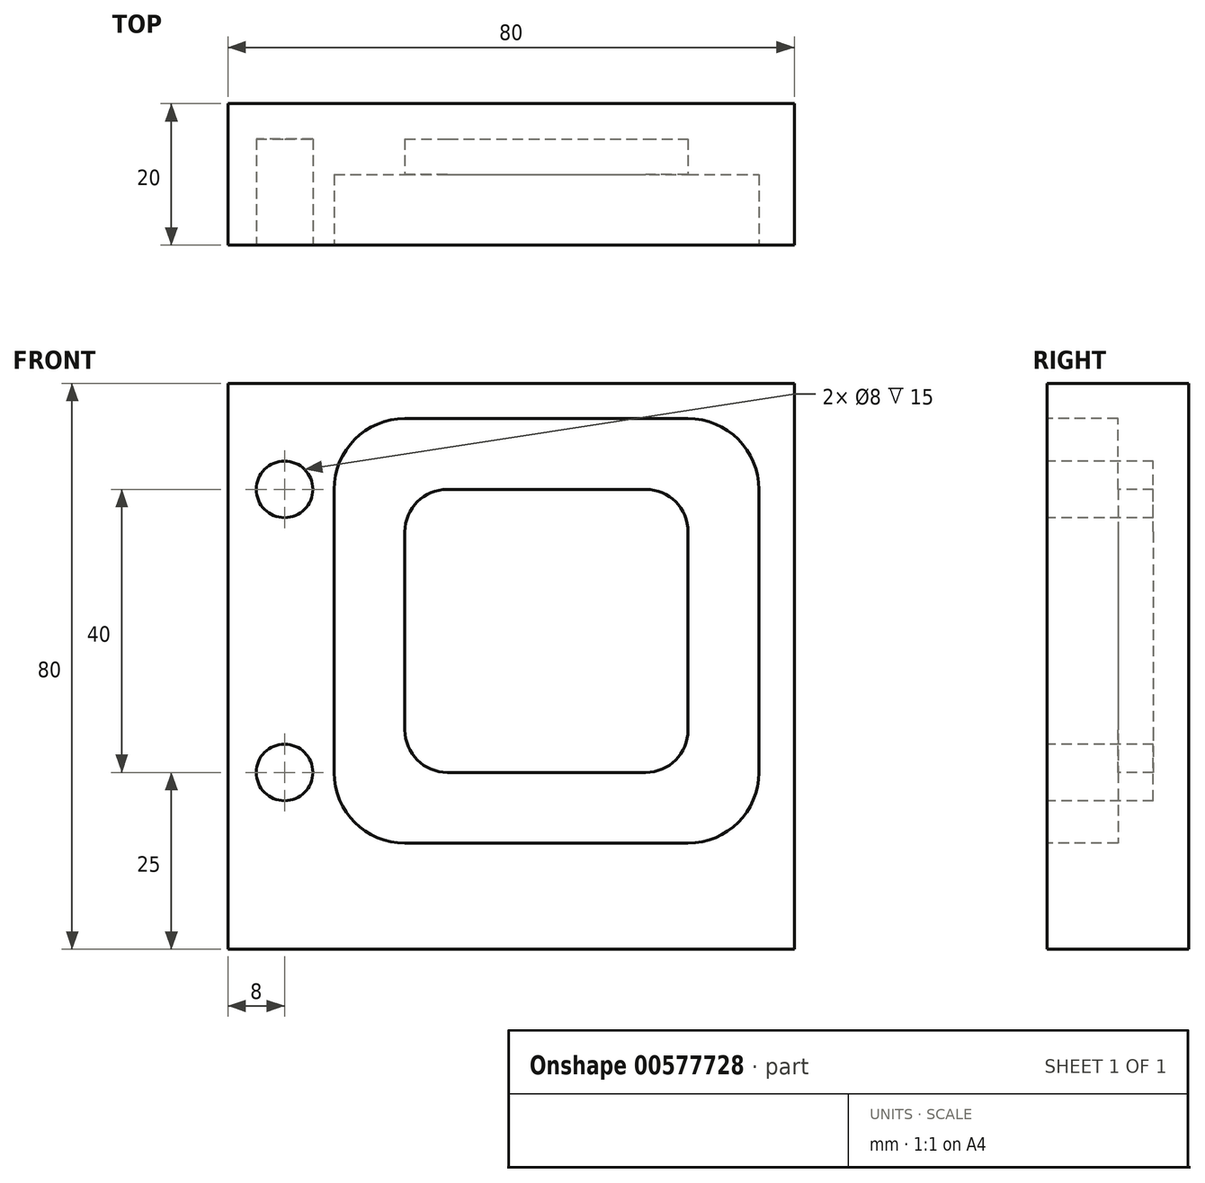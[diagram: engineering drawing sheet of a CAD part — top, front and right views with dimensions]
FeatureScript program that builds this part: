
annotation { "Feature Type Name" : "Feature", "Feature Type Description" : "" }
export const myFeature = defineFeature(function(context is Context, id is Id, definition is map)
    precondition{}
    {
        {
            var Q0;
            Q0=qCreatedBy(makeId("Front.planeOp"),FACE);
            var sketch = newSketch(context, id + "F0", { "sketchPlane" : qUnion([Q0])});
            skLineSegment(sketch, "E0.bottom", {"start": v(0, 0) * mm, "end": v(-80, 0) * mm});
            skLineSegment(sketch, "E0.top", {"start": v(0, 80) * mm, "end": v(-80, 80) * mm});
            skLineSegment(sketch, "E0.left", {"start": v(0, 0) * mm, "end": v(0, 80) * mm});
            skLineSegment(sketch, "E0.right", {"start": v(-80, 0) * mm, "end": v(-80, 80) * mm});
            skSolve(sketch);
        }
        {
            var Q0;
            Q0=makeQuery(id+"F0.imprint","IMPRINT",FACE,{"disambiguationData":[TD([[makeQuery(id+"F0.imprint","IMPRINT",EDGE,{"derivedFrom":sQuery(id+"F0.wireOp",EDGE,"E0.bottom")}),-1.0]])]});
            extrude(context, id + "F1", {"entities" : qUnion([Q0]), "depth" : 20 * mm, "offsetDistance" : 25 * mm});
        }
        {
            var Q0;
            Q0=makeQuery(id+"F1.opExtrude","CAP_FACE",FACE,{"disambiguationData":[OSD([sQuery(id+"F0.wireOp",EDGE,"E0.bottom"),sQuery(id+"F0.wireOp",EDGE,"E0.top"),sQuery(id+"F0.wireOp",EDGE,"E0.left"),sQuery(id+"F0.wireOp",EDGE,"E0.right")])],"isStart":false});
            var sketch = newSketch(context, id + "F2", { "sketchPlane" : qUnion([Q0])});
            skLineSegment(sketch, "E1", {"start": v(-55, 75) * mm, "end": v(-15, 75) * mm});
            skLineSegment(sketch, "E2", {"start": v(-65, 65) * mm, "end": v(-65, 25) * mm});
            skLineSegment(sketch, "E3", {"start": v(-55, 15) * mm, "end": v(-15, 15) * mm});
            skLineSegment(sketch, "E4", {"start": v(-5, 65) * mm, "end": v(-5, 25) * mm});
            skArc(sketch, "E5", {"start": v(-55, 75) * mm, "mid": v(-62.07, 72.07) * mm, "end": v(-65, 65) * mm});
            skArc(sketch, "E6", {"start": v(-65, 25) * mm, "mid": v(-62.07, 17.93) * mm, "end": v(-55, 15) * mm});
            skArc(sketch, "E7", {"start": v(-15, 15) * mm, "mid": v(-7.93, 17.93) * mm, "end": v(-5, 25) * mm});
            skArc(sketch, "E8", {"start": v(-5, 65) * mm, "mid": v(-7.93, 72.07) * mm, "end": v(-15, 75) * mm});
            skSolve(sketch);
        }
        {
            var Q0;
            Q0=makeQuery(id+"F2.imprint","IMPRINT",FACE,{"disambiguationData":[TD([[makeQuery(id+"F2.imprint","IMPRINT",EDGE,{"derivedFrom":sQuery(id+"F2.wireOp",EDGE,"E1")}),-1.0]])]});
            extrude(context, id + "F3", {"entities" : qUnion([Q0]), "operationType" : NewBodyOperationType.REMOVE, "oppositeDirection" : true, "depth" : 10 * mm, "offsetDistance" : 25 * mm});
        }
        {
            var Q0;
            Q0=makeQuery(id+"F3.boolean.opBoolean","COPY",FACE,{"derivedFrom":makeQuery(id+"F3.opExtrude","CAP_FACE",FACE,{"disambiguationData":[OSD([sQuery(id+"F2.wireOp",EDGE,"E1"),sQuery(id+"F2.wireOp",EDGE,"E2"),sQuery(id+"F2.wireOp",EDGE,"E3"),sQuery(id+"F2.wireOp",EDGE,"E4"),sQuery(id+"F2.wireOp",EDGE,"E5"),sQuery(id+"F2.wireOp",EDGE,"E6"),sQuery(id+"F2.wireOp",EDGE,"E7"),sQuery(id+"F2.wireOp",EDGE,"E8")])],"isStart":false})});
            var sketch = newSketch(context, id + "F4", { "sketchPlane" : qUnion([Q0])});
            skLineSegment(sketch, "E9", {"start": v(-49, 65) * mm, "end": v(-21, 65) * mm});
            skLineSegment(sketch, "E10", {"start": v(-55, 59) * mm, "end": v(-55, 31) * mm});
            skLineSegment(sketch, "E11", {"start": v(-49, 25) * mm, "end": v(-21, 25) * mm});
            skLineSegment(sketch, "E12", {"start": v(-15, 59) * mm, "end": v(-15, 31) * mm});
            skArc(sketch, "E13", {"start": v(-49, 65) * mm, "mid": v(-53.24, 63.24) * mm, "end": v(-55, 59) * mm});
            skArc(sketch, "E14", {"start": v(-55, 31) * mm, "mid": v(-53.24, 26.76) * mm, "end": v(-49, 25) * mm});
            skArc(sketch, "E15", {"start": v(-21, 25) * mm, "mid": v(-16.76, 26.76) * mm, "end": v(-15, 31) * mm});
            skArc(sketch, "E16", {"start": v(-15, 59) * mm, "mid": v(-16.76, 63.24) * mm, "end": v(-21, 65) * mm});
            skSolve(sketch);
        }
        {
            var Q0;
            Q0 = qSketchRegion(id + "F4", true);
            extrude(context, id + "F5", {"entities" : qUnion([Q0]), "operationType" : NewBodyOperationType.REMOVE, "oppositeDirection" : true, "depth" : 5 * mm, "offsetDistance" : 25 * mm});
        }
        {
            var Q0;
            Q0=makeQuery(id+"F1.opExtrude","CAP_FACE",FACE,{"disambiguationData":[OSD([sQuery(id+"F0.wireOp",EDGE,"E0.bottom"),sQuery(id+"F0.wireOp",EDGE,"E0.top"),sQuery(id+"F0.wireOp",EDGE,"E0.left"),sQuery(id+"F0.wireOp",EDGE,"E0.right")])],"isStart":false});
            var sketch = newSketch(context, id + "F6", { "sketchPlane" : qUnion([Q0])});
            skCircle(sketch, "E17", {"center": v(-72, 65) * mm, "radius": 4 * mm});
            skCircle(sketch, "E18", {"center": v(-72, 25) * mm, "radius": 4 * mm});
            skSolve(sketch);
        }
        {
            var Q0;
            Q0 = qSketchRegion(id + "F6", true);
            extrude(context, id + "F7", {"entities" : qUnion([Q0]), "operationType" : NewBodyOperationType.REMOVE, "oppositeDirection" : true, "depth" : 15 * mm, "offsetDistance" : 25 * mm});
        }
    });
